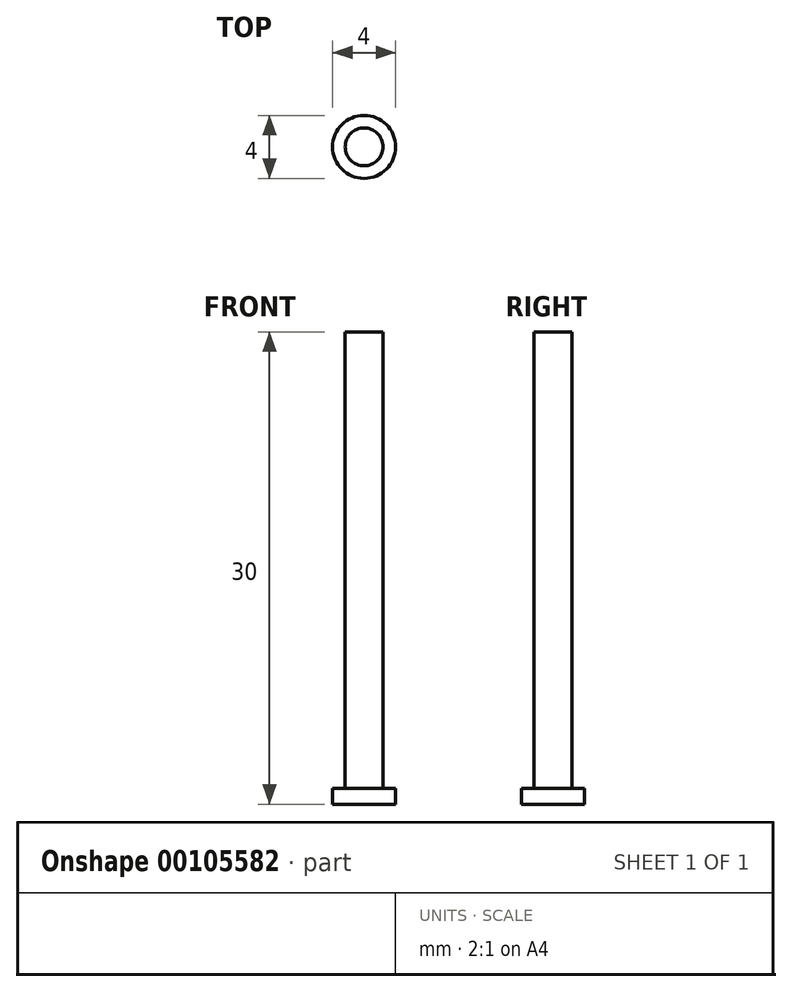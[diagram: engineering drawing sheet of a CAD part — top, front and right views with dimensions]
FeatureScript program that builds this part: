
annotation { "Feature Type Name" : "Feature", "Feature Type Description" : "" }
export const myFeature = defineFeature(function(context is Context, id is Id, definition is map)
    precondition{}
    {
        {
            var Q0;
            Q0=qCreatedBy(makeId("Front.planeOp"),FACE);
            var sketch = newSketch(context, id + "F0", { "sketchPlane" : qUnion([Q0])});
            skLineSegment(sketch, "E0.bottom", {"start": v(0, 21.08) * mm, "end": v(1.2, 21.08) * mm});
            skLineSegment(sketch, "E0.top", {"start": v(0, -7.92) * mm, "end": v(1.2, -7.92) * mm});
            skLineSegment(sketch, "E0.left", {"start": v(0, 21.08) * mm, "end": v(0, -7.92) * mm});
            skLineSegment(sketch, "E0.right", {"start": v(1.2, 21.08) * mm, "end": v(1.2, -7.92) * mm});
            skLineSegment(sketch, "E1.bottom", {"start": v(0, -7.92) * mm, "end": v(2, -7.92) * mm});
            skLineSegment(sketch, "E1.top", {"start": v(0, -8.92) * mm, "end": v(2, -8.92) * mm});
            skLineSegment(sketch, "E1.left", {"start": v(0, -7.92) * mm, "end": v(0, -8.92) * mm});
            skLineSegment(sketch, "E1.right", {"start": v(2, -7.92) * mm, "end": v(2, -8.92) * mm});
            skSolve(sketch);
        }
        {
            var Q0;
            Q0=makeQuery(id+"F0.imprint","IMPRINT",FACE,{"disambiguationData":[TD([[makeQuery(id+"F0.imprint","IMPRINT",EDGE,{"derivedFrom":sQuery(id+"F0.wireOp",EDGE,"E1.top")}),1.0]])]});
            var Q1;
            Q1=makeQuery(id+"F0.imprint","IMPRINT",FACE,{"disambiguationData":[TD([[makeQuery(id+"F0.imprint","IMPRINT",EDGE,{"derivedFrom":sQuery(id+"F0.wireOp",EDGE,"E0.bottom")}),-1.0]])]});
            var Q2;
            Q2=sQuery(id+"F0.wireOp",EDGE,"E0.left");
            revolve(context, id + "F1", {"entities" : qUnion([Q0, Q1]), "axis" : qUnion([Q2]), "revolveType" : RevolveType.FULL});
        }
    });
